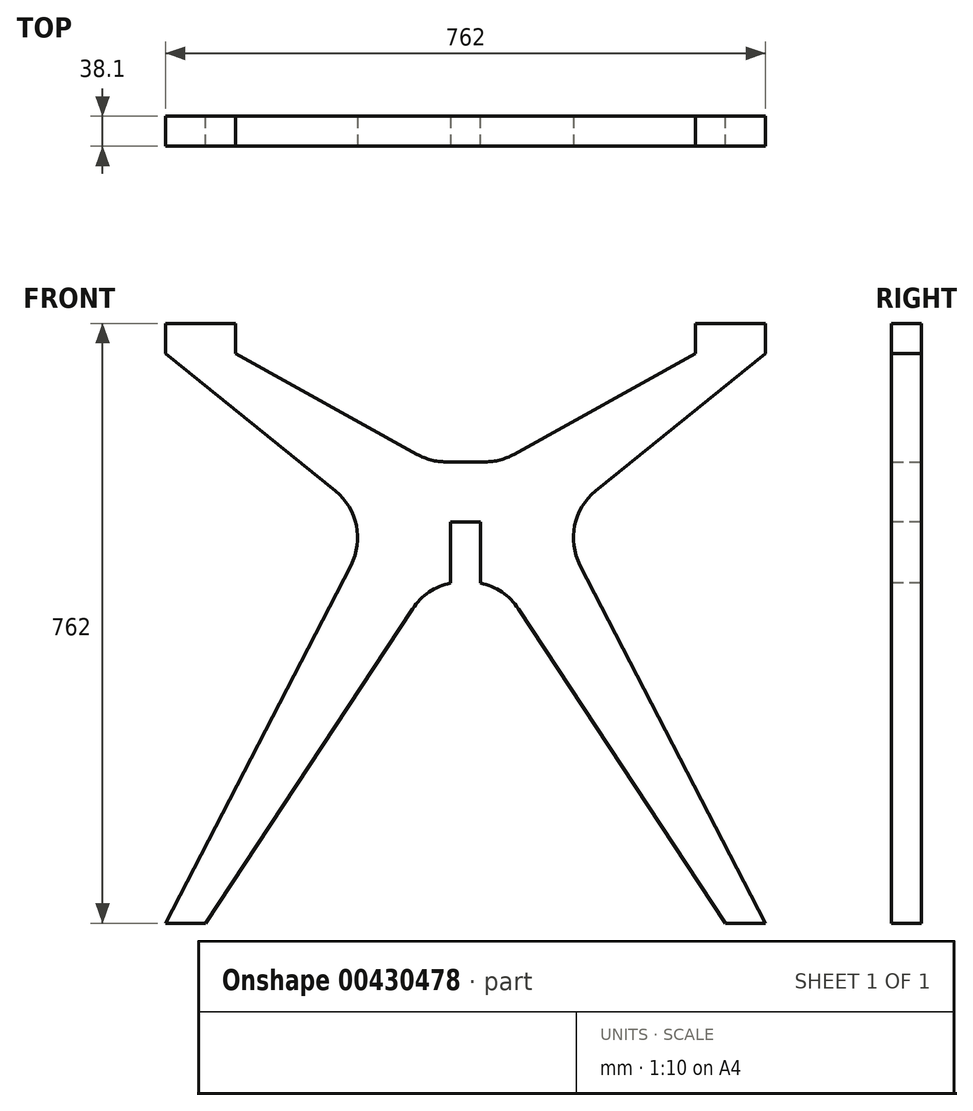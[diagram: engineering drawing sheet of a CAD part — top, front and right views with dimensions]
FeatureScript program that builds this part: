
annotation { "Feature Type Name" : "Feature", "Feature Type Description" : "" }
export const myFeature = defineFeature(function(context is Context, id is Id, definition is map)
    precondition{}
    {
        {
            var Q0;
            Q0=qCreatedBy(makeId("Front.planeOp"),FACE);
            var sketch = newSketch(context, id + "F0", { "sketchPlane" : qUnion([Q0])});
            skLineSegment(sketch, "E0", {"start": v(0, 0) * mm, "end": v(0, 630.74) * mm, "construction": true});
            skLineSegment(sketch, "E1", {"start": v(-19.05, 0) * mm, "end": v(-44.45, 0) * mm});
            skLineSegment(sketch, "E2", {"start": v(-44.45, 0) * mm, "end": v(-330.2, -433.69) * mm});
            skLineSegment(sketch, "E3", {"start": v(-330.2, -433.69) * mm, "end": v(-381, -433.69) * mm});
            skLineSegment(sketch, "E4", {"start": v(-381, -433.69) * mm, "end": v(-117.02, 76.2) * mm});
            skLineSegment(sketch, "E5", {"start": v(-117.02, 76.2) * mm, "end": v(-381, 290.21) * mm});
            skLineSegment(sketch, "E6", {"start": v(-381, 290.21) * mm, "end": v(-292.1, 290.21) * mm});
            skLineSegment(sketch, "E7", {"start": v(-292.1, 290.21) * mm, "end": v(-44.45, 152.4) * mm});
            skLineSegment(sketch, "E8", {"start": v(-44.45, 152.4) * mm, "end": v(0, 152.4) * mm});
            skLineSegment(sketch, "E9.MirrorCS", {"start": v(330.2, -433.69) * mm, "end": v(381, -433.69) * mm});
            skLineSegment(sketch, "E10.MirrorCS", {"start": v(19.05, 0) * mm, "end": v(44.45, 0) * mm});
            skLineSegment(sketch, "E11.MirrorCS", {"start": v(381, 290.21) * mm, "end": v(292.1, 290.21) * mm});
            skLineSegment(sketch, "E12.MirrorCS", {"start": v(117.02, 76.2) * mm, "end": v(381, 290.21) * mm});
            skLineSegment(sketch, "E13.MirrorCS", {"start": v(44.45, 152.4) * mm, "end": v(0, 152.4) * mm});
            skLineSegment(sketch, "E14.MirrorCS", {"start": v(44.45, 0) * mm, "end": v(330.2, -433.69) * mm});
            skLineSegment(sketch, "E15.MirrorCS", {"start": v(292.1, 290.21) * mm, "end": v(44.45, 152.4) * mm});
            skLineSegment(sketch, "E16.MirrorCS", {"start": v(381, -433.69) * mm, "end": v(117.02, 76.2) * mm});
            skLineSegment(sketch, "E17", {"start": v(-19.05, 0) * mm, "end": v(-19.05, 76.2) * mm, "construction": true});
            skLineSegment(sketch, "E18", {"start": v(-19.05, 76.2) * mm, "end": v(0, 76.2) * mm, "construction": true});
            skLineSegment(sketch, "E19", {"start": v(0, 76.2) * mm, "end": v(19.05, 76.2) * mm, "construction": true});
            skLineSegment(sketch, "E20", {"start": v(19.05, 76.2) * mm, "end": v(19.05, 0) * mm, "construction": true});
            skPoint(sketch, "E21.orphan", {"position": v(0, 0) * mm});
            skLineSegment(sketch, "E22", {"start": v(-19.05, 0) * mm, "end": v(19.05, 0) * mm});
            skLineSegment(sketch, "E23", {"start": v(-19.05, 152.4) * mm, "end": v(-19.05, 76.2) * mm, "construction": true});
            skLineSegment(sketch, "E24", {"start": v(19.05, 76.2) * mm, "end": v(19.05, 152.4) * mm, "construction": true});
            skSolve(sketch);
        }
        {
            var Q0;
            Q0=makeQuery(id+"F0.imprint","IMPRINT",FACE,{"disambiguationData":[TD([[makeQuery(id+"F0.imprint","IMPRINT",EDGE,{"derivedFrom":sQuery(id+"F0.wireOp",EDGE,"E1")}),-1.0]])]});
            extrude(context, id + "F1", {"entities" : qUnion([Q0]), "endBound" : BoundingType.SYMMETRIC, "depth" : 38.1 * mm});
        }
        {
            var Q0;
            Q0=makeQuery(id+"F1.opExtrude","SWEPT_EDGE",EDGE,{"disambiguationData":[OSD([sQuery(id+"F0.wireOp",EDGE,"E12.MirrorCS"),sQuery(id+"F0.wireOp",EDGE,"E16.MirrorCS")])]});
            var Q1;
            Q1=makeQuery(id+"F1.opExtrude","SWEPT_EDGE",EDGE,{"disambiguationData":[OSD([sQuery(id+"F0.wireOp",EDGE,"E7"),sQuery(id+"F0.wireOp",EDGE,"E8")])]});
            var Q2;
            Q2=makeQuery(id+"F1.opExtrude","SWEPT_EDGE",EDGE,{"disambiguationData":[OSD([sQuery(id+"F0.wireOp",EDGE,"E13.MirrorCS"),sQuery(id+"F0.wireOp",EDGE,"E15.MirrorCS")])]});
            var Q3;
            Q3=makeQuery(id+"F1.opExtrude","SWEPT_EDGE",EDGE,{"disambiguationData":[OSD([sQuery(id+"F0.wireOp",EDGE,"E4"),sQuery(id+"F0.wireOp",EDGE,"E5")])]});
            var Q4;
            Q4=makeQuery(id+"F1.opExtrude","SWEPT_EDGE",EDGE,{"disambiguationData":[OSD([sQuery(id+"F0.wireOp",EDGE,"E1"),sQuery(id+"F0.wireOp",EDGE,"E2")])]});
            var Q5;
            Q5=makeQuery(id+"F1.opExtrude","SWEPT_EDGE",EDGE,{"disambiguationData":[OSD([sQuery(id+"F0.wireOp",EDGE,"E10.MirrorCS"),sQuery(id+"F0.wireOp",EDGE,"E14.MirrorCS")])]});
            fillet(context, id + "F2", {"entities" : qUnion([Q0, Q1, Q2, Q3, Q4, Q5]), "radius" : 76.2 * mm, "tangentPropagation" : true, "allowEdgeOverflow" : false});
        }
        {
            var Q0;
            Q0=makeQuery(id+"F1.opExtrude","SWEPT_FACE",FACE,{"disambiguationData":[OSD([sQuery(id+"F0.wireOp",EDGE,"E11.MirrorCS")])]});
            var sketch = newSketch(context, id + "F3", { "sketchPlane" : qUnion([Q0])});
            skLineSegment(sketch, "E25.0", {"start": v(292.1, -19.05) * mm, "end": v(292.1, 19.05) * mm});
            skLineSegment(sketch, "E26.0", {"start": v(381, 19.05) * mm, "end": v(292.1, 19.05) * mm});
            skLineSegment(sketch, "E27.0", {"start": v(381, -19.05) * mm, "end": v(381, 19.05) * mm});
            skLineSegment(sketch, "E28.0", {"start": v(381, -19.05) * mm, "end": v(292.1, -19.05) * mm});
            skLineSegment(sketch, "E29.0", {"start": v(-292.1, -19.05) * mm, "end": v(-292.1, 19.05) * mm});
            skLineSegment(sketch, "E30.0", {"start": v(-381, 19.05) * mm, "end": v(-292.1, 19.05) * mm});
            skLineSegment(sketch, "E31.0", {"start": v(-381, -19.05) * mm, "end": v(-381, 19.05) * mm});
            skLineSegment(sketch, "E32.0", {"start": v(-381, -19.05) * mm, "end": v(-292.1, -19.05) * mm});
            skSolve(sketch);
        }
        {
            var Q0;
            Q0=makeQuery(id+"F3.imprint","IMPRINT",FACE,{"disambiguationData":[TD([[makeQuery(id+"F3.imprint","IMPRINT",EDGE,{"derivedFrom":sQuery(id+"F3.wireOp",EDGE,"E29.0")}),1.0]])]});
            var Q1;
            Q1=makeQuery(id+"F3.imprint","IMPRINT",FACE,{"disambiguationData":[TD([[makeQuery(id+"F3.imprint","IMPRINT",EDGE,{"derivedFrom":sQuery(id+"F3.wireOp",EDGE,"E25.0")}),-1.0]])]});
            extrude(context, id + "F4", {"entities" : qUnion([Q0, Q1]), "operationType" : NewBodyOperationType.ADD, "depth" : 38.1 * mm});
        }
        {
            var Q0;
            Q0=makeQuery(id+"F4.boolean.opBoolean","MERGE",FACE,{"derivedFrom":[makeQuery(id+"F1.opExtrude","CAP_FACE",FACE,{"disambiguationData":[OSD([sQuery(id+"F0.wireOp",EDGE,"E1"),sQuery(id+"F0.wireOp",EDGE,"E2"),sQuery(id+"F0.wireOp",EDGE,"E3"),sQuery(id+"F0.wireOp",EDGE,"E4"),sQuery(id+"F0.wireOp",EDGE,"E5"),sQuery(id+"F0.wireOp",EDGE,"E6"),sQuery(id+"F0.wireOp",EDGE,"E7"),sQuery(id+"F0.wireOp",EDGE,"E8"),sQuery(id+"F0.wireOp",EDGE,"E9.MirrorCS"),sQuery(id+"F0.wireOp",EDGE,"E10.MirrorCS"),sQuery(id+"F0.wireOp",EDGE,"E11.MirrorCS"),sQuery(id+"F0.wireOp",EDGE,"E12.MirrorCS"),sQuery(id+"F0.wireOp",EDGE,"E13.MirrorCS"),sQuery(id+"F0.wireOp",EDGE,"E14.MirrorCS"),sQuery(id+"F0.wireOp",EDGE,"E15.MirrorCS"),sQuery(id+"F0.wireOp",EDGE,"E16.MirrorCS"),sQuery(id+"F0.wireOp",EDGE,"E22")])],"isStart":false}),makeQuery(id+"F4.opExtrude","SWEPT_FACE",FACE,{"disambiguationData":[OSD([sQuery(id+"F3.wireOp",EDGE,"E28.0")])]}),makeQuery(id+"F4.opExtrude","SWEPT_FACE",FACE,{"disambiguationData":[OSD([sQuery(id+"F3.wireOp",EDGE,"E32.0")])]})]});
            var sketch = newSketch(context, id + "F5", { "sketchPlane" : qUnion([Q0])});
            skLineSegment(sketch, "E33.bottom", {"start": v(-19.05, -12.7) * mm, "end": v(19.05, -12.7) * mm});
            skLineSegment(sketch, "E33.top", {"start": v(-19.05, 76.2) * mm, "end": v(19.05, 76.2) * mm});
            skLineSegment(sketch, "E33.left", {"start": v(-19.05, -12.7) * mm, "end": v(-19.05, 76.2) * mm});
            skLineSegment(sketch, "E33.right", {"start": v(19.05, -12.7) * mm, "end": v(19.05, 76.2) * mm});
            skSolve(sketch);
        }
        {
            var Q0;
            {var subQ4=sQuery(id+"F5.wireOp",EDGE,"E33.top");Q0=makeQuery(id+"F5.imprint","IMPRINT",FACE,{"disambiguationData":[TD([[makeQuery(id+"F5.imprint","IMPRINT",EDGE,{"derivedFrom":subQ4}),-1.0]])]});}
            var Q1;
            {var subQ1=sQuery(id+"F5.wireOp",EDGE,"E33.bottom");Q1=makeQuery(id+"F5.imprint","IMPRINT",FACE,{"disambiguationData":[TD([[makeQuery(id+"F5.imprint","IMPRINT",EDGE,{"derivedFrom":subQ1}),1.0]])]});}
            extrude(context, id + "F6", {"entities" : qUnion([Q0, Q1]), "operationType" : NewBodyOperationType.REMOVE, "endBound" : BoundingType.THROUGH_ALL, "oppositeDirection" : true, "depth" : 25.4 * mm});
        }
    });
